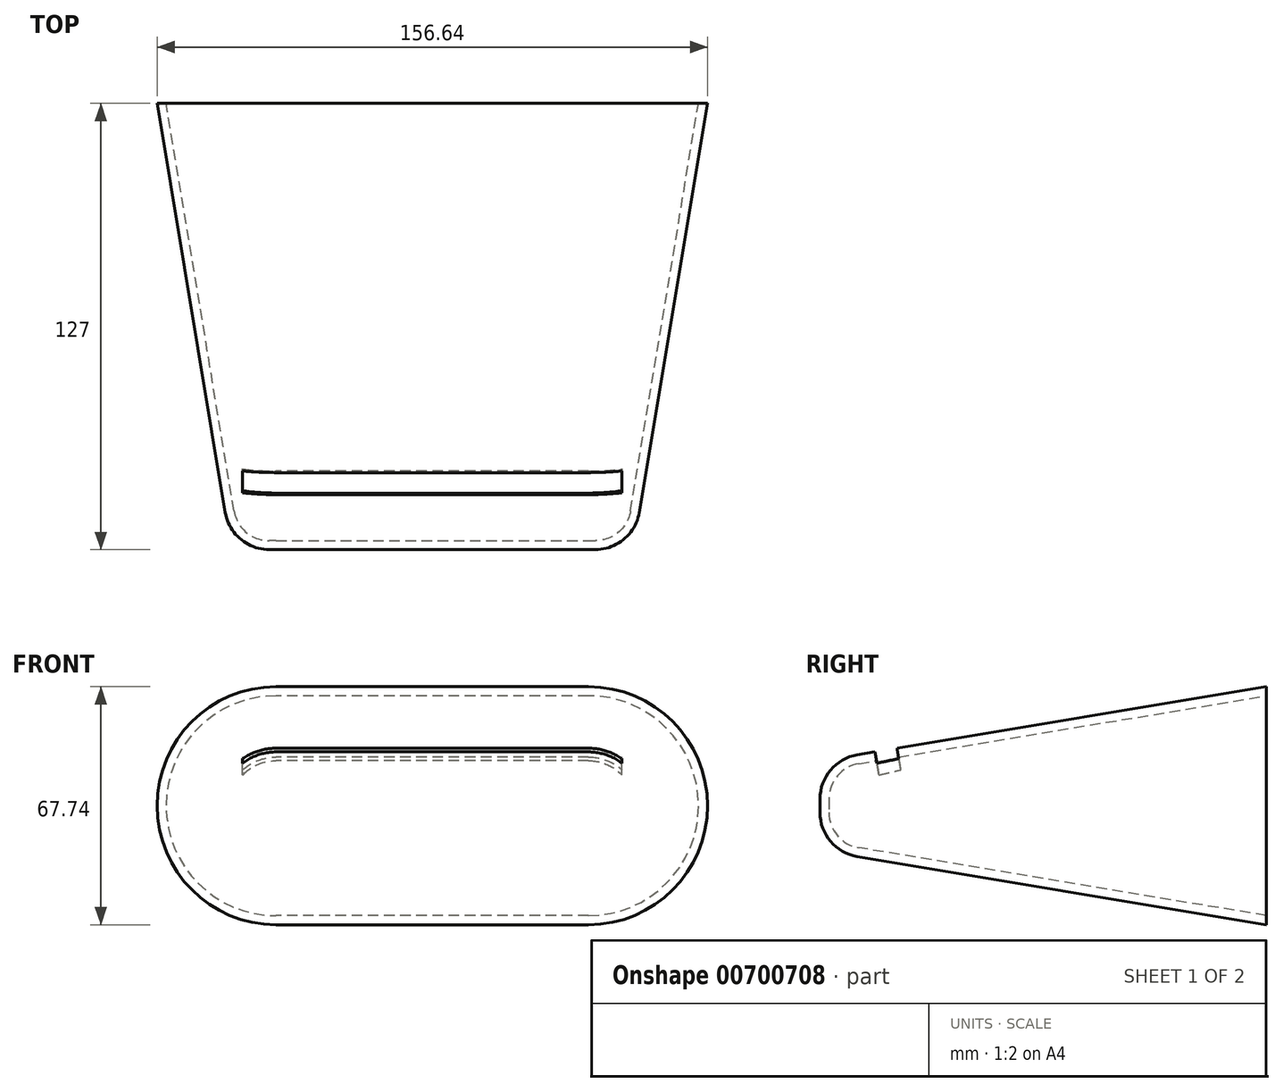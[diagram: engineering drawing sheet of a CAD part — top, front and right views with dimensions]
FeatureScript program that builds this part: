
annotation { "Feature Type Name" : "Feature", "Feature Type Description" : "" }
export const myFeature = defineFeature(function(context is Context, id is Id, definition is map)
    precondition{}
    {
        {
            var Q0;
            Q0=qCreatedBy(makeId("Front.planeOp"),FACE);
            var sketch = newSketch(context, id + "F0", { "sketchPlane" : qUnion([Q0])});
            skLineSegment(sketch, "E0.bottom", {"start": v(82.55, 38.1) * mm, "end": v(-82.55, 38.1) * mm});
            skLineSegment(sketch, "E0.top", {"start": v(82.55, -38.1) * mm, "end": v(-82.55, -38.1) * mm});
            skLineSegment(sketch, "E0.left", {"start": v(82.55, 38.1) * mm, "end": v(82.55, -38.1) * mm});
            skLineSegment(sketch, "E0.right", {"start": v(-82.55, 38.1) * mm, "end": v(-82.55, -38.1) * mm});
            skPoint(sketch, "E0.middle", {"position": v(0, 0) * mm});
            skSolve(sketch);
        }
        {
            var Q0;
            Q0=makeQuery(id+"F0.imprint","IMPRINT",FACE,{"disambiguationData":[TD([[makeQuery(id+"F0.imprint","IMPRINT",EDGE,{"derivedFrom":sQuery(id+"F0.wireOp",EDGE,"E0.bottom")}),1.0]])]});
            extrude(context, id + "F1", {"entities" : qUnion([Q0]), "oppositeDirection" : true, "depth" : 127 * mm, "offsetDistance" : 25.4 * mm});
        }
        {
            var Q0;
            Q0=makeQuery(id+"F1.opExtrude","SWEPT_EDGE",EDGE,{"disambiguationData":[OSD([sQuery(id+"F0.wireOp",EDGE,"E0.bottom"),sQuery(id+"F0.wireOp",EDGE,"E0.left")])]});
            var Q1;
            Q1=makeQuery(id+"F1.opExtrude","SWEPT_EDGE",EDGE,{"disambiguationData":[OSD([sQuery(id+"F0.wireOp",EDGE,"E0.top"),sQuery(id+"F0.wireOp",EDGE,"E0.left")])]});
            var Q2;
            Q2=makeQuery(id+"F1.opExtrude","SWEPT_EDGE",EDGE,{"disambiguationData":[OSD([sQuery(id+"F0.wireOp",EDGE,"E0.top"),sQuery(id+"F0.wireOp",EDGE,"E0.right")])]});
            var Q3;
            Q3=makeQuery(id+"F1.opExtrude","SWEPT_EDGE",EDGE,{"disambiguationData":[OSD([sQuery(id+"F0.wireOp",EDGE,"E0.bottom"),sQuery(id+"F0.wireOp",EDGE,"E0.right")])]});
            fillet(context, id + "F2", {"entities" : qUnion([Q0, Q1, Q2, Q3]), "radius" : 38.1 * mm, "tangentPropagation" : true, "allowEdgeOverflow" : false});
        }
        {
            var Q0;
            Q0=makeQuery(id+"F1.opExtrude","CAP_EDGE",EDGE,{"disambiguationData":[OSD([sQuery(id+"F0.wireOp",EDGE,"E0.bottom")])],"isStart":true});
            chamfer(context, id + "F3", {"entities" : qUnion([Q0]), "chamferType" : ChamferType.TWO_OFFSETS, "width1" : 25.4 * mm, "oppositeDirection" : false, "width2" : 152.4 * mm, "tangentPropagation" : true});
        }
        {
            var Q0;
            Q0=makeQuery(id+"F3.opChamfer","BLEND_FACE",FACE,{"disambiguationData":[OSD([sQuery(id+"F0.wireOp",EDGE,"E0.bottom")])]});
            var sketch = newSketch(context, id + "F4", { "sketchPlane" : qUnion([Q0])});
            skLineSegment(sketch, "E1.bottom", {"start": v(53.98, 24.31) * mm, "end": v(-53.98, 24.31) * mm});
            skLineSegment(sketch, "E1.top", {"start": v(53.98, 17.96) * mm, "end": v(-53.98, 17.96) * mm});
            skLineSegment(sketch, "E1.left", {"start": v(53.98, 24.31) * mm, "end": v(53.98, 17.96) * mm});
            skLineSegment(sketch, "E1.right", {"start": v(-53.98, 24.31) * mm, "end": v(-53.98, 17.96) * mm});
            skPoint(sketch, "E1.middle", {"position": v(0, 21.14) * mm});
            skSolve(sketch);
        }
        {
            var Q0;
            {var subQ0=sQuery(id+"F0.wireOp",EDGE,"E0.bottom");Q0=makeQuery(id+"F3.opChamfer","BLEND_EDGE",EDGE,{"blendedFrom":[makeQuery(id+"F1.opExtrude","CAP_EDGE",EDGE,{"disambiguationData":[OSD([subQ0])],"isStart":true}),makeQuery(id+"F1.opExtrude","CAP_FACE",FACE,{"disambiguationData":[OSD([subQ0,sQuery(id+"F0.wireOp",EDGE,"E0.top"),sQuery(id+"F0.wireOp",EDGE,"E0.left"),sQuery(id+"F0.wireOp",EDGE,"E0.right")])],"isStart":true})],"blendedInto":[makeQuery(id+"F1.opExtrude","CAP_FACE",FACE,{"disambiguationData":[OSD([subQ0,sQuery(id+"F0.wireOp",EDGE,"E0.top"),sQuery(id+"F0.wireOp",EDGE,"E0.left"),sQuery(id+"F0.wireOp",EDGE,"E0.right")])],"isStart":true})]});}
            fillet(context, id + "F5", {"entities" : qUnion([Q0]), "radius" : 12.7 * mm, "tangentPropagation" : true, "allowEdgeOverflow" : false});
        }
        {
            var Q0;
            Q0=makeQuery(id+"F1.opExtrude","CAP_FACE",FACE,{"disambiguationData":[OSD([sQuery(id+"F0.wireOp",EDGE,"E0.bottom"),sQuery(id+"F0.wireOp",EDGE,"E0.top"),sQuery(id+"F0.wireOp",EDGE,"E0.left"),sQuery(id+"F0.wireOp",EDGE,"E0.right")])],"isStart":false});
            shell(context, id + "F6", {"entities" : qUnion([Q0]), "thickness" : 2.54 * mm});
        }
        {
            var Q0;
            Q0 = qSketchRegion(id + "F4", true);
            extrude(context, id + "F7", {"entities" : qUnion([Q0]), "operationType" : NewBodyOperationType.REMOVE, "endBound" : BoundingType.UP_TO_NEXT, "oppositeDirection" : true, "depth" : 25.4 * mm, "offsetDistance" : 25.4 * mm});
        }
    });
